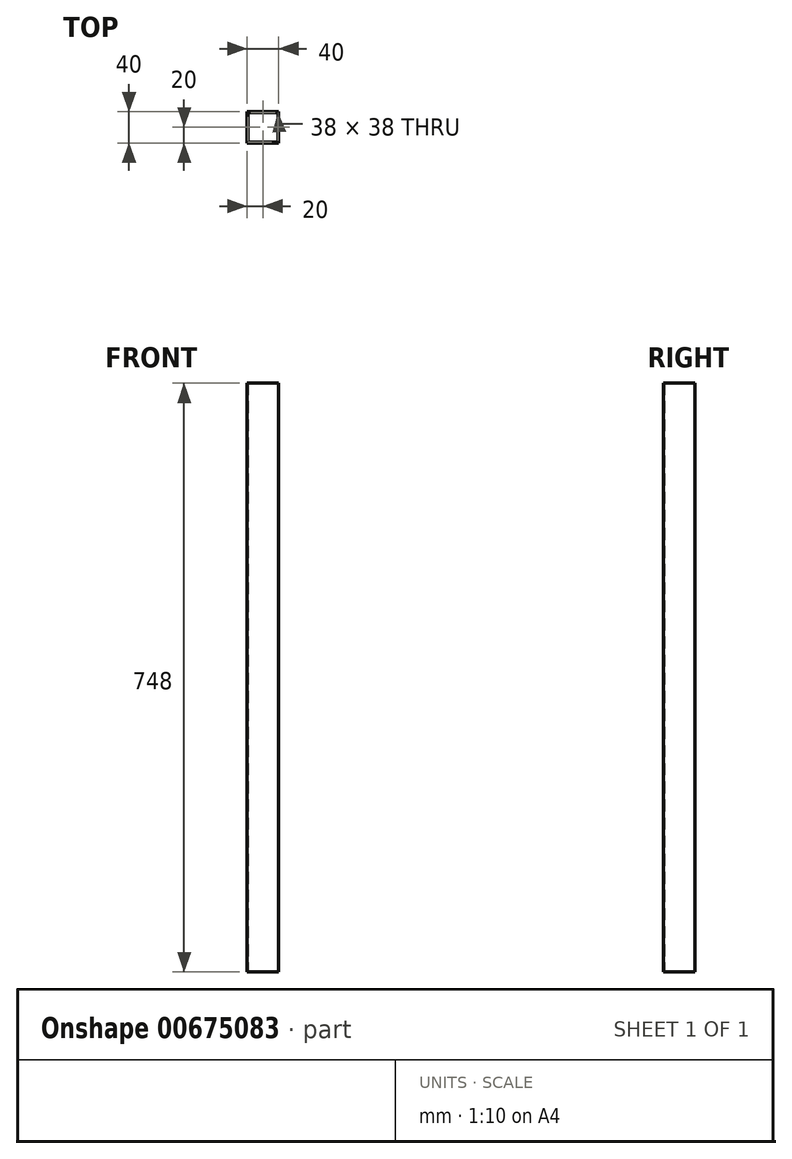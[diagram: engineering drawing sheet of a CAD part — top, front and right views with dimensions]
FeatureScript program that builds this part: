
annotation { "Feature Type Name" : "Feature", "Feature Type Description" : "" }
export const myFeature = defineFeature(function(context is Context, id is Id, definition is map)
    precondition{}
    {
        {
            var Q0;
            Q0=qCreatedBy(makeId("Top.planeOp"),FACE);
            var sketch = newSketch(context, id + "F0", { "sketchPlane" : qUnion([Q0])});
            skLineSegment(sketch, "E0.bottom", {"start": v(19, 19) * mm, "end": v(-19, 19) * mm});
            skLineSegment(sketch, "E0.top", {"start": v(19, -19) * mm, "end": v(-19, -19) * mm});
            skLineSegment(sketch, "E0.left", {"start": v(19, 19) * mm, "end": v(19, -19) * mm});
            skLineSegment(sketch, "E0.right", {"start": v(-19, 19) * mm, "end": v(-19, -19) * mm});
            skPoint(sketch, "E0.middle", {"position": v(0, 0) * mm});
            skLineSegment(sketch, "E1.bottom", {"start": v(20, 20) * mm, "end": v(-20, 20) * mm});
            skLineSegment(sketch, "E1.top", {"start": v(20, -20) * mm, "end": v(-20, -20) * mm});
            skLineSegment(sketch, "E1.left", {"start": v(20, 20) * mm, "end": v(20, -20) * mm});
            skLineSegment(sketch, "E1.right", {"start": v(-20, 20) * mm, "end": v(-20, -20) * mm});
            skSolve(sketch);
        }
        {
            var Q0;
            Q0=makeQuery(id+"F0.imprint","IMPRINT",FACE,{"disambiguationData":[TD([[makeQuery(id+"F0.imprint","IMPRINT",EDGE,{"derivedFrom":sQuery(id+"F0.wireOp",EDGE,"E0.bottom")}),-1.0]])]});
            extrude(context, id + "F1", {"entities" : qUnion([Q0]), "depth" : (750 - 2) * mm, "offsetDistance" : 25 * mm});
        }
    });
